# Revit family: Haworth_Hi-Pad_Chair
name_source: partatom
category: Furniture
revit_build: Autodesk Revit 2018 (Build: 20170223_1515(x64)
units: mm (PartAtom-declared; Revit-internal decimal feet)

## family parameters
Always vertical = Yes
Cut with Voids When Loaded = No
OmniClass Number = 23.40.70.14.64.21
OmniClass Title = Systems Furniture
Room Calculation Point = No
Shared = No
Work Plane-Based = No

## types (1)
- Chair
    Actual Depth = 21"
    Actual Height = 32"
    Actual Width = 17"
    Assembly Code = E2020200
    Bar Height = 11 7/8"
    Bar Position Width = 12 1/2"
    Base Depth Bottom = 18"
    Base Depth Top = 13"
    Base Width Bottom = 16"
    Base Width Top = 11"
    Description = Haworth_Chair_Hi-Pad_Chair
    Frame Finish = Haworth - Metal - Steel
    Glide Finish = Haworth - Paint - Metallic Champagne
    Manufacturer = Haworth
    Model = Haworth_Chair_Hi-Pad_Chair
    Revision Number = 1
    Seat Finish = Haworth - Leather - Pelle - Grigio 70-0GR
    Size = Verify Final Dim. w/ Haworth
    Sustainability Info = www.haworth.com/en-us/About-Us/Sustainability/Pages/Vision.aspx
    Top Frame Back = 15"
    Top Frame Front = 16 1/2"
    URL = http://haworthcollection.com
    URL - Product = http://haworthcollection.com
    Warranty = http://haworthcollection.com

## geometry (parser evidence)
native form markers: Blend x6, Sweep x4
no freeform markers — native parametric forms only
